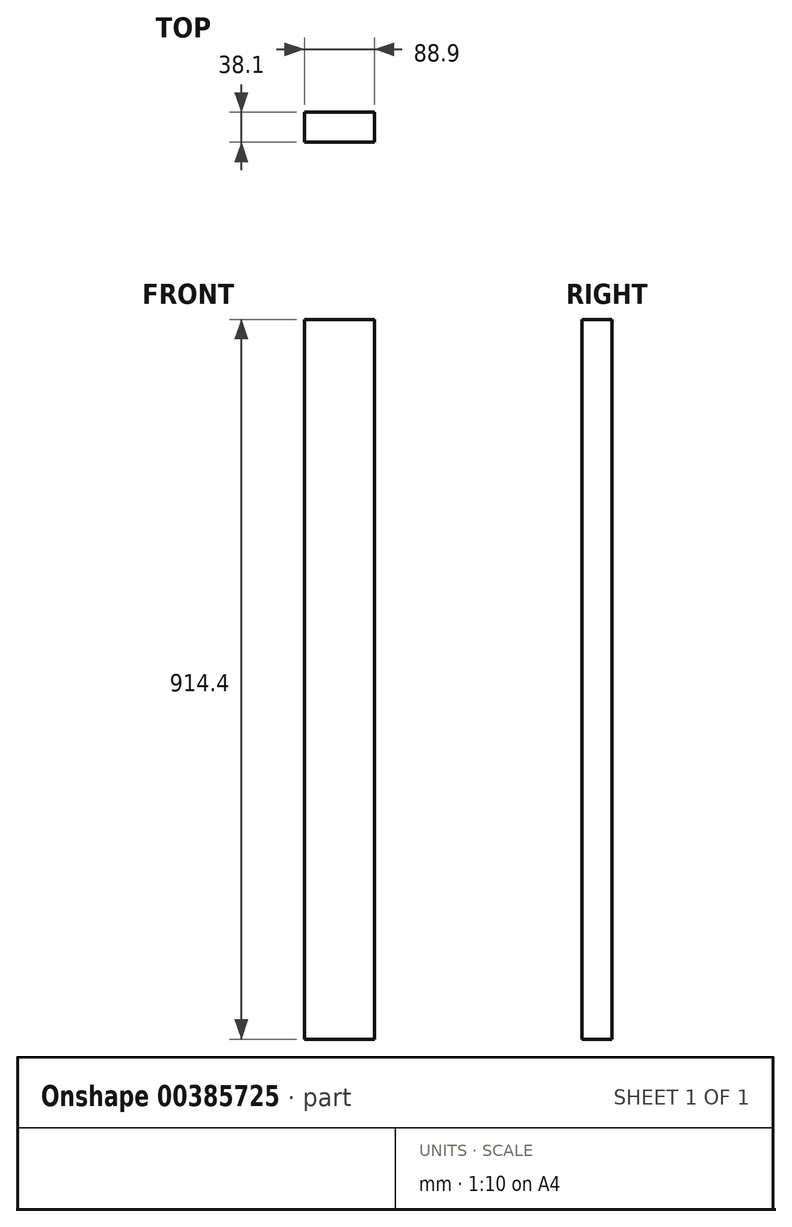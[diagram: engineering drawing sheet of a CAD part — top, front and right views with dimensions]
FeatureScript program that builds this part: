
annotation { "Feature Type Name" : "Feature", "Feature Type Description" : "" }
export const myFeature = defineFeature(function(context is Context, id is Id, definition is map)
    precondition{}
    {
        {
            var Q0;
            Q0=qCreatedBy(makeId("Top.planeOp"),FACE);
            var sketch = newSketch(context, id + "F0", { "sketchPlane" : qUnion([Q0])});
            skLineSegment(sketch, "E0.bottom", {"start": v(44.45, 19.05) * mm, "end": v(-44.45, 19.05) * mm});
            skLineSegment(sketch, "E0.top", {"start": v(44.45, -19.05) * mm, "end": v(-44.45, -19.05) * mm});
            skLineSegment(sketch, "E0.left", {"start": v(44.45, 19.05) * mm, "end": v(44.45, -19.05) * mm});
            skLineSegment(sketch, "E0.right", {"start": v(-44.45, 19.05) * mm, "end": v(-44.45, -19.05) * mm});
            skPoint(sketch, "E0.middle", {"position": v(0, 0) * mm});
            skSolve(sketch);
        }
        {
            var Q0;
            Q0=makeQuery(id+"F0.imprint","IMPRINT",FACE,{"disambiguationData":[TD([[makeQuery(id+"F0.imprint","IMPRINT",EDGE,{"derivedFrom":sQuery(id+"F0.wireOp",EDGE,"E0.bottom")}),1.0]])]});
            extrude(context, id + "F1", {"entities" : qUnion([Q0]), "depth" : 914.4 * mm});
        }
    });
